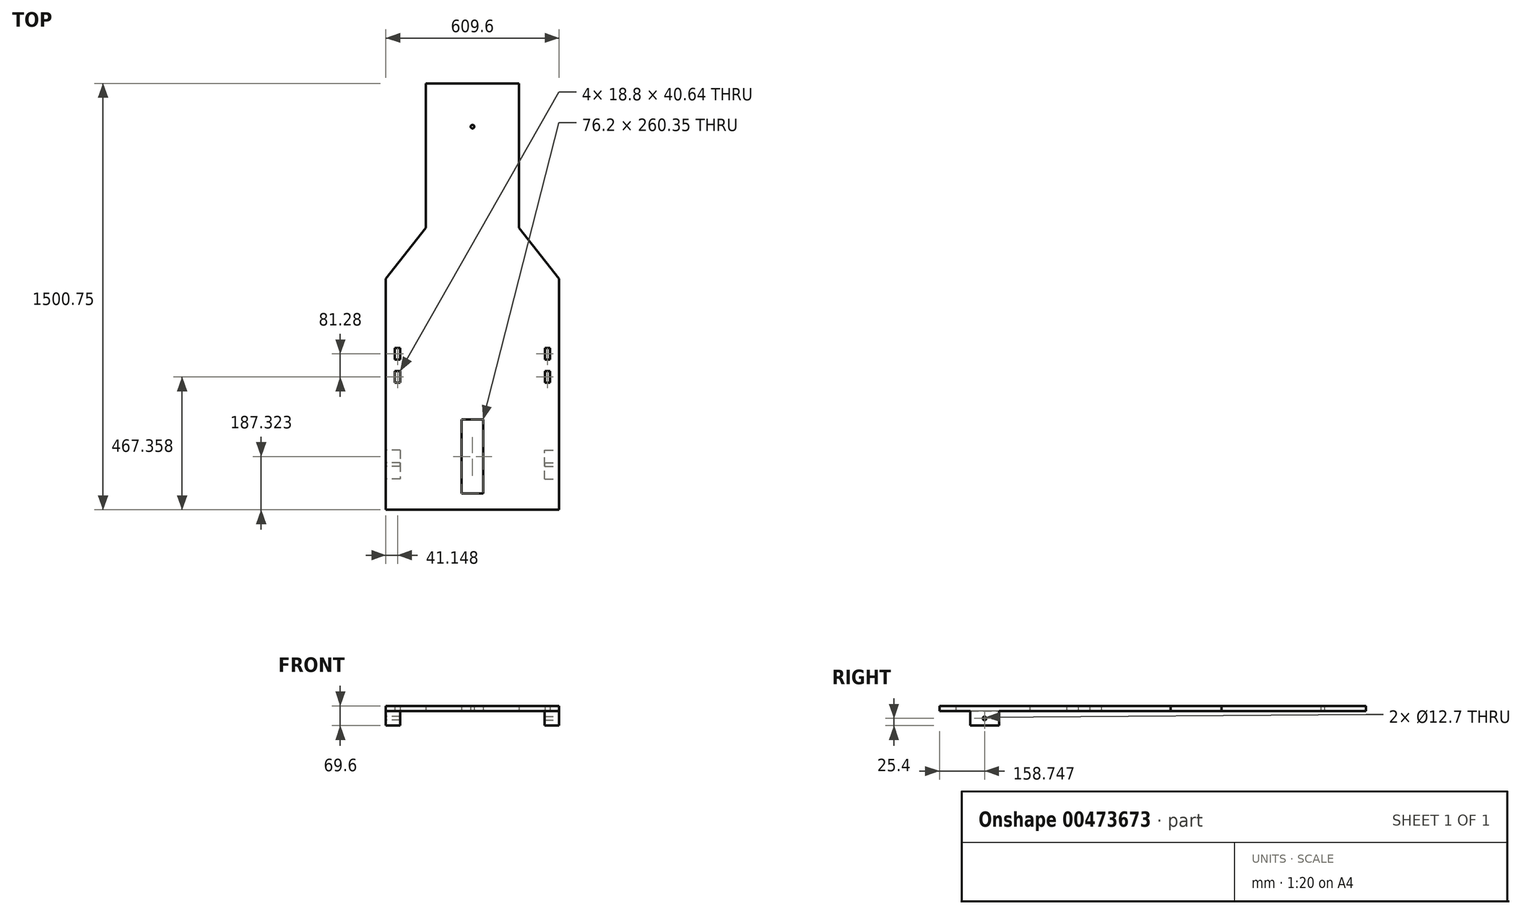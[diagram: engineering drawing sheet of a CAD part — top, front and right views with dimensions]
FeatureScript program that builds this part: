
annotation { "Feature Type Name" : "Feature", "Feature Type Description" : "" }
export const myFeature = defineFeature(function(context is Context, id is Id, definition is map)
    precondition{}
    {
        {
            var Q0;
            Q0=qCreatedBy(makeId("Top.planeOp"),FACE);
            var sketch = newSketch(context, id + "F0", { "sketchPlane" : qUnion([Q0])});
            skLineSegment(sketch, "E0", {"start": v(-304.8, 526.29) * mm, "end": v(-163.82, 706.24) * mm});
            skLineSegment(sketch, "E1.MirrorCS", {"start": v(304.8, 526.29) * mm, "end": v(163.82, 706.24) * mm});
            skLineSegment(sketch, "E2", {"start": v(-163.82, 706.24) * mm, "end": v(-163.82, 1214.24) * mm});
            skLineSegment(sketch, "E3", {"start": v(163.82, 706.24) * mm, "end": v(163.82, 1214.24) * mm});
            skLineSegment(sketch, "E4", {"start": v(163.82, 1214.24) * mm, "end": v(-163.82, 1214.24) * mm});
            skLineSegment(sketch, "E5", {"start": v(0, 1068.19) * mm, "end": v(0, 1061.84) * mm});
            skPoint(sketch, "E5.endSnap0", {"position": v(0, 1214.24) * mm});
            skCircle(sketch, "E6", {"center": v(0, 1061.84) * mm, "radius": 6.35 * mm});
            skLineSegment(sketch, "E7", {"start": v(0, 1068.19) * mm, "end": v(0, 1055.49) * mm});
            skLineSegment(sketch, "E8", {"start": v(-304.8, 526.29) * mm, "end": v(-304.8, -286.51) * mm});
            skLineSegment(sketch, "E9", {"start": v(-304.8, -286.51) * mm, "end": v(304.8, -286.51) * mm});
            skLineSegment(sketch, "E10", {"start": v(304.8, -286.51) * mm, "end": v(304.8, 526.29) * mm});
            skLineSegment(sketch, "E11", {"start": v(-304.8, 30.99) * mm, "end": v(-304.8, -286.51) * mm});
            skLineSegment(sketch, "E12", {"start": v(304.8, 30.99) * mm, "end": v(304.8, -286.51) * mm});
            skLineSegment(sketch, "E13", {"start": v(304.8, -286.51) * mm, "end": v(304.8, 30.99) * mm});
            skPoint(sketch, "E14", {"position": v(-304.8, 119.89) * mm});
            skPoint(sketch, "E15", {"position": v(304.8, 119.89) * mm});
            skLineSegment(sketch, "E16", {"start": v(-273.05, 160.53) * mm, "end": v(-254.25, 160.53) * mm});
            skLineSegment(sketch, "E17", {"start": v(-254.25, 160.53) * mm, "end": v(-254.25, 201.17) * mm});
            skLineSegment(sketch, "E18", {"start": v(-254.25, 201.17) * mm, "end": v(-273.05, 201.17) * mm});
            skLineSegment(sketch, "E19", {"start": v(-273.05, 201.17) * mm, "end": v(-273.05, 160.53) * mm});
            skLineSegment(sketch, "E20", {"start": v(-273.05, 241.8) * mm, "end": v(-254.25, 241.8) * mm});
            skLineSegment(sketch, "E21", {"start": v(-254.25, 241.8) * mm, "end": v(-254.25, 282.45) * mm});
            skLineSegment(sketch, "E22", {"start": v(-254.25, 282.45) * mm, "end": v(-273.05, 282.45) * mm});
            skLineSegment(sketch, "E23", {"start": v(-273.05, 282.45) * mm, "end": v(-273.05, 241.8) * mm});
            skLineSegment(sketch, "E24.MirrorCS", {"start": v(254.25, 160.53) * mm, "end": v(254.25, 201.17) * mm});
            skLineSegment(sketch, "E25.MirrorCS", {"start": v(254.25, 201.17) * mm, "end": v(273.05, 201.17) * mm});
            skLineSegment(sketch, "E26.MirrorCS", {"start": v(273.05, 201.17) * mm, "end": v(273.05, 160.53) * mm});
            skLineSegment(sketch, "E27.MirrorCS", {"start": v(273.05, 160.53) * mm, "end": v(254.25, 160.53) * mm});
            skLineSegment(sketch, "E28.MirrorCS", {"start": v(273.05, 241.8) * mm, "end": v(254.25, 241.8) * mm});
            skLineSegment(sketch, "E29.MirrorCS", {"start": v(254.25, 241.8) * mm, "end": v(254.25, 282.45) * mm});
            skLineSegment(sketch, "E30.MirrorCS", {"start": v(254.25, 282.45) * mm, "end": v(273.05, 282.45) * mm});
            skLineSegment(sketch, "E31.MirrorCS", {"start": v(273.05, 282.45) * mm, "end": v(273.05, 241.8) * mm});
            skPoint(sketch, "E32", {"position": v(304.8, -228.45) * mm});
            skLineSegment(sketch, "E33", {"start": v(38.1, -229.36) * mm, "end": v(-38.1, -229.36) * mm});
            skLineSegment(sketch, "E34", {"start": v(-38.1, 30.99) * mm, "end": v(38.1, 30.99) * mm});
            skLineSegment(sketch, "E35", {"start": v(0, 30.99) * mm, "end": v(-38.1, 30.99) * mm});
            skLineSegment(sketch, "E36", {"start": v(-38.1, 30.99) * mm, "end": v(0, 30.99) * mm});
            skLineSegment(sketch, "E37", {"start": v(0, 30.99) * mm, "end": v(38.1, 30.99) * mm});
            skLineSegment(sketch, "E38", {"start": v(38.1, 30.99) * mm, "end": v(38.1, -229.36) * mm});
            skLineSegment(sketch, "E39", {"start": v(-38.1, -229.36) * mm, "end": v(-38.1, 30.99) * mm});
            skPoint(sketch, "E40.start.orphan", {"position": v(-228.6, 30.99) * mm});
            skPoint(sketch, "E41.orphan", {"position": v(228.6, 30.99) * mm});
            skSolve(sketch);
        }
        {
            var Q0;
            Q0=makeQuery(id+"F0.imprint","IMPRINT",FACE,{"disambiguationData":[TD([[makeQuery(id+"F0.imprint","IMPRINT",EDGE,{"derivedFrom":sQuery(id+"F0.wireOp",EDGE,"E0")}),-1.0]])]});
            var Q1;
            Q1=makeQuery(id+"F0.imprint","IMPRINT",FACE,{"disambiguationData":[TD([[makeQuery(id+"F0.imprint","IMPRINT",EDGE,{"derivedFrom":sQuery(id+"F0.wireOp",EDGE,"pcyciWPa-pX1M-HQCH-51zv-ISjyDSHkGuuB")}),-1.0]])]});
            var Q2;
            Q2=makeQuery(id+"F0.imprint","IMPRINT",FACE,{"disambiguationData":[TD([[makeQuery(id+"F0.imprint","IMPRINT",EDGE,{"derivedFrom":sQuery(id+"F0.wireOp",EDGE,"KcpJDcPN-6GkO-Zn21-V98P-4AsIVuYR6ghy")}),1.0]])]});
            extrude(context, id + "F1", {"entities" : qUnion([Q0, Q1, Q2]), "depth" : 18.8 * mm});
        }
        {
            var Q0;
            Q0=makeQuery(id+"F1.opExtrude","SWEPT_FACE",FACE,{"disambiguationData":[OSD([sQuery(id+"F0.wireOp",EDGE,"E10"),sQuery(id+"F0.wireOp",EDGE,"E12")])]});
            var sketch = newSketch(context, id + "F2", { "sketchPlane" : qUnion([Q0])});
            skLineSegment(sketch, "E42", {"start": v(-286.51, 0) * mm, "end": v(30.99, 0) * mm});
            skLineSegment(sketch, "E43", {"start": v(30.99, 0) * mm, "end": v(-127.76, 0) * mm});
            skLineSegment(sketch, "E44", {"start": v(-127.76, -50.8) * mm, "end": v(-178.56, -50.8) * mm});
            skLineSegment(sketch, "E45", {"start": v(-178.56, -50.8) * mm, "end": v(-178.56, 0) * mm});
            skLineSegment(sketch, "E46", {"start": v(-178.56, 0) * mm, "end": v(-127.76, 0) * mm});
            skLineSegment(sketch, "E47", {"start": v(-127.76, 0) * mm, "end": v(-76.96, 0) * mm});
            skLineSegment(sketch, "E48", {"start": v(-76.96, 0) * mm, "end": v(-76.96, -50.8) * mm});
            skLineSegment(sketch, "E49", {"start": v(-76.96, -50.8) * mm, "end": v(-127.76, -50.8) * mm});
            skLineSegment(sketch, "E50", {"start": v(-178.56, 0) * mm, "end": v(-76.96, 0) * mm});
            skCircle(sketch, "E51", {"center": v(-127.76, -25.4) * mm, "radius": 6.35 * mm});
            skPoint(sketch, "E51.centerSnap0", {"position": v(-178.56, -25.4) * mm});
            skSolve(sketch);
        }
        {
            var Q0;
            Q0 = qSketchRegion(id + "F2", true);
            extrude(context, id + "F3", {"entities" : qUnion([Q0]), "operationType" : NewBodyOperationType.ADD, "oppositeDirection" : true, "depth" : 50.8 * mm, "offsetDistance" : 25.4 * mm});
        }
        {
            var Q0;
            Q0=makeQuery(id+"F1.opExtrude","SWEPT_FACE",FACE,{"disambiguationData":[OSD([sQuery(id+"F0.wireOp",EDGE,"E8"),sQuery(id+"F0.wireOp",EDGE,"E11")])]});
            var sketch = newSketch(context, id + "F4", { "sketchPlane" : qUnion([Q0])});
            skLineSegment(sketch, "E52", {"start": v(76.96, 0) * mm, "end": v(76.96, -50.8) * mm});
            skLineSegment(sketch, "E53", {"start": v(76.96, -50.8) * mm, "end": v(178.56, -50.8) * mm});
            skLineSegment(sketch, "E54", {"start": v(178.56, -50.8) * mm, "end": v(178.56, 0) * mm});
            skLineSegment(sketch, "E55", {"start": v(178.56, 0) * mm, "end": v(76.96, 0) * mm});
            skCircle(sketch, "E56", {"center": v(127.76, -25.4) * mm, "radius": 6.35 * mm});
            skPoint(sketch, "E56.centerSnap0", {"position": v(127.76, 0) * mm});
            skPoint(sketch, "E56.centerSnap1", {"position": v(178.56, -25.4) * mm});
            skSolve(sketch);
        }
        {
            var Q0;
            Q0=makeQuery(id+"F4.imprint","IMPRINT",FACE,{"disambiguationData":[TD([[makeQuery(id+"F4.imprint","IMPRINT",EDGE,{"derivedFrom":sQuery(id+"F4.wireOp",EDGE,"E52")}),1.0]])]});
            extrude(context, id + "F5", {"entities" : qUnion([Q0]), "operationType" : NewBodyOperationType.ADD, "oppositeDirection" : true, "depth" : 50.8 * mm});
        }
    });
